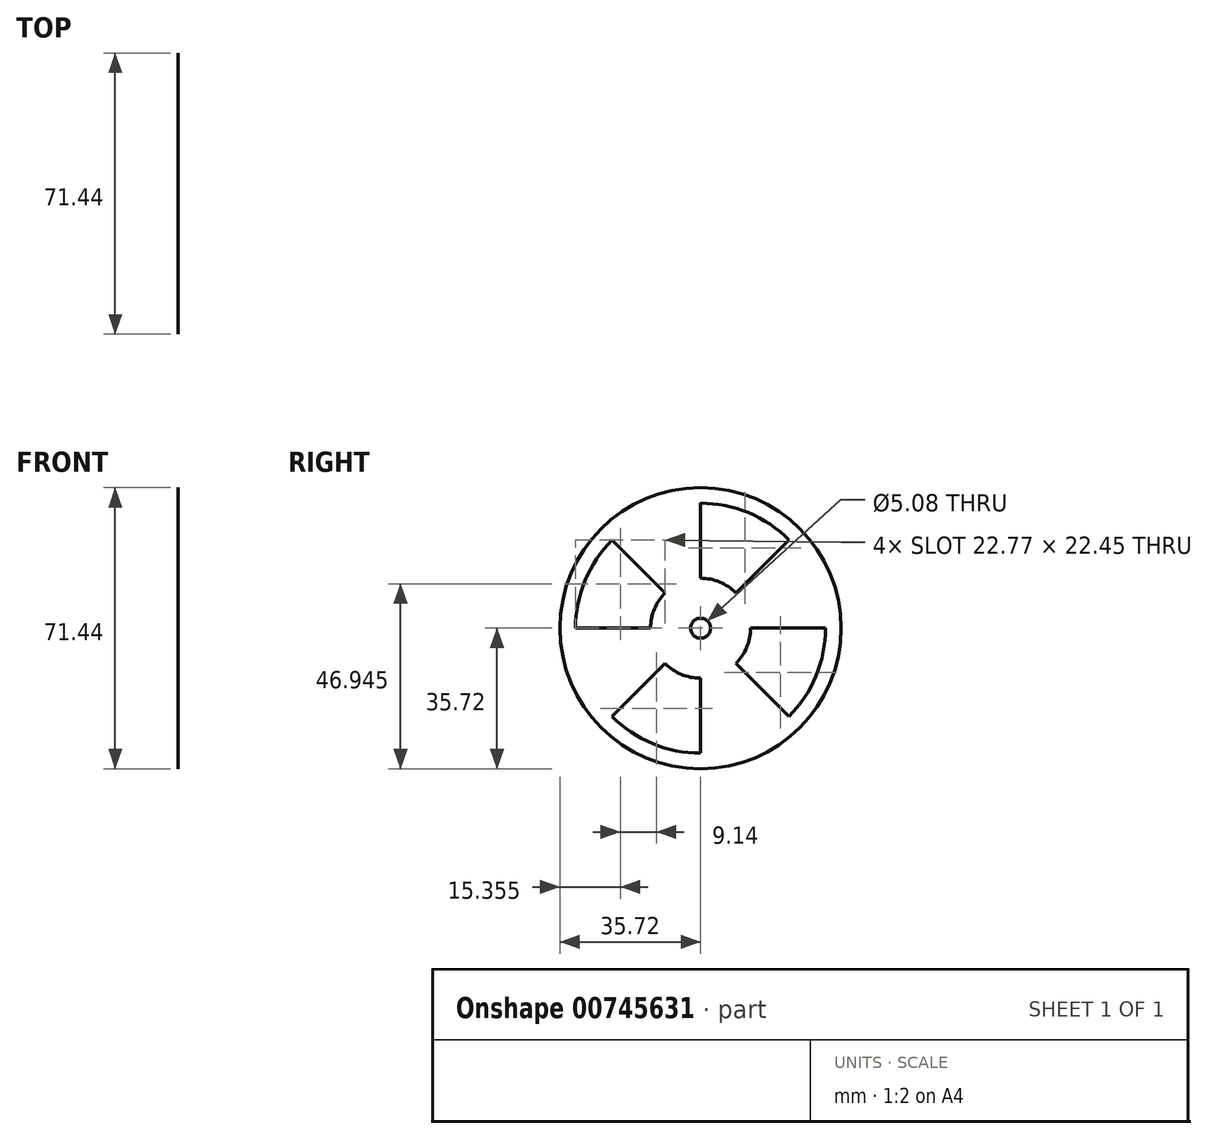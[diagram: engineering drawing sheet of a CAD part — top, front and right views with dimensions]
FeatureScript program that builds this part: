
annotation { "Feature Type Name" : "Feature", "Feature Type Description" : "" }
export const myFeature = defineFeature(function(context is Context, id is Id, definition is map)
    precondition{}
    {
        {
            var Q0;
            Q0=qCreatedBy(makeId("Right.planeOp"),FACE);
            var sketch = newSketch(context, id + "F0", { "sketchPlane" : qUnion([Q0])});
            skCircle(sketch, "E0", {"center": v(0, 0) * mm, "radius": 35.72 * mm});
            skArc(sketch, "E1", {"start": v(-22.45, -22.45) * mm, "mid": v(-12.15, -29.33) * mm, "end": v(0, -31.75) * mm});
            skLineSegment(sketch, "E2", {"start": v(0, 12.7) * mm, "end": v(0, 31.75) * mm});
            skLineSegment(sketch, "E3", {"start": v(8.98, 8.98) * mm, "end": v(22.45, 22.45) * mm});
            skLineSegment(sketch, "E4", {"start": v(12.7, 0) * mm, "end": v(31.75, 0) * mm});
            skLineSegment(sketch, "E5", {"start": v(-12.7, 0) * mm, "end": v(-31.75, 0) * mm});
            skLineSegment(sketch, "E6", {"start": v(-8.98, 8.98) * mm, "end": v(-22.45, 22.45) * mm});
            skLineSegment(sketch, "E7", {"start": v(0, -12.7) * mm, "end": v(0, -31.75) * mm});
            skLineSegment(sketch, "E8", {"start": v(8.98, -8.98) * mm, "end": v(22.45, -22.45) * mm});
            skLineSegment(sketch, "E9", {"start": v(-8.98, -8.98) * mm, "end": v(-22.45, -22.45) * mm});
            skArc(sketch, "E10", {"start": v(-8.98, 8.98) * mm, "mid": v(-11.73, 4.86) * mm, "end": v(-12.7, 0) * mm});
            skArc(sketch, "E11.trimOffspring", {"start": v(8.98, 8.98) * mm, "mid": v(4.86, 11.73) * mm, "end": v(0, 12.7) * mm});
            skArc(sketch, "E12.trimOffspring", {"start": v(8.98, -8.98) * mm, "mid": v(11.73, -4.86) * mm, "end": v(12.7, 0) * mm});
            skArc(sketch, "E13.trimOffspring", {"start": v(-8.98, -8.98) * mm, "mid": v(-4.86, -11.73) * mm, "end": v(0, -12.7) * mm});
            skArc(sketch, "E14.trimOffspring", {"start": v(22.45, -22.45) * mm, "mid": v(29.33, -12.15) * mm, "end": v(31.75, 0) * mm});
            skArc(sketch, "E15.trimOffspring", {"start": v(22.45, 22.45) * mm, "mid": v(12.15, 29.33) * mm, "end": v(0, 31.75) * mm});
            skArc(sketch, "E16.trimOffspring", {"start": v(-22.45, 22.45) * mm, "mid": v(-29.33, 12.15) * mm, "end": v(-31.75, 0) * mm});
            skCircle(sketch, "E17", {"center": v(0, 0) * mm, "radius": 2.54 * mm});
            skSolve(sketch);
        }
        {
            var Q0;
            Q0=makeQuery(id+"F0.imprint","IMPRINT",FACE,{"disambiguationData":[TD([[makeQuery(id+"F0.imprint","IMPRINT",EDGE,{"derivedFrom":sQuery(id+"F0.wireOp",EDGE,"E0")}),1.0]])]});
            extrude(context, id + "F1", {"entities" : qUnion([Q0]), "depth" : 1 / 203.2 * mm, "offsetDistance" : 25.4 * mm});
        }
    });
